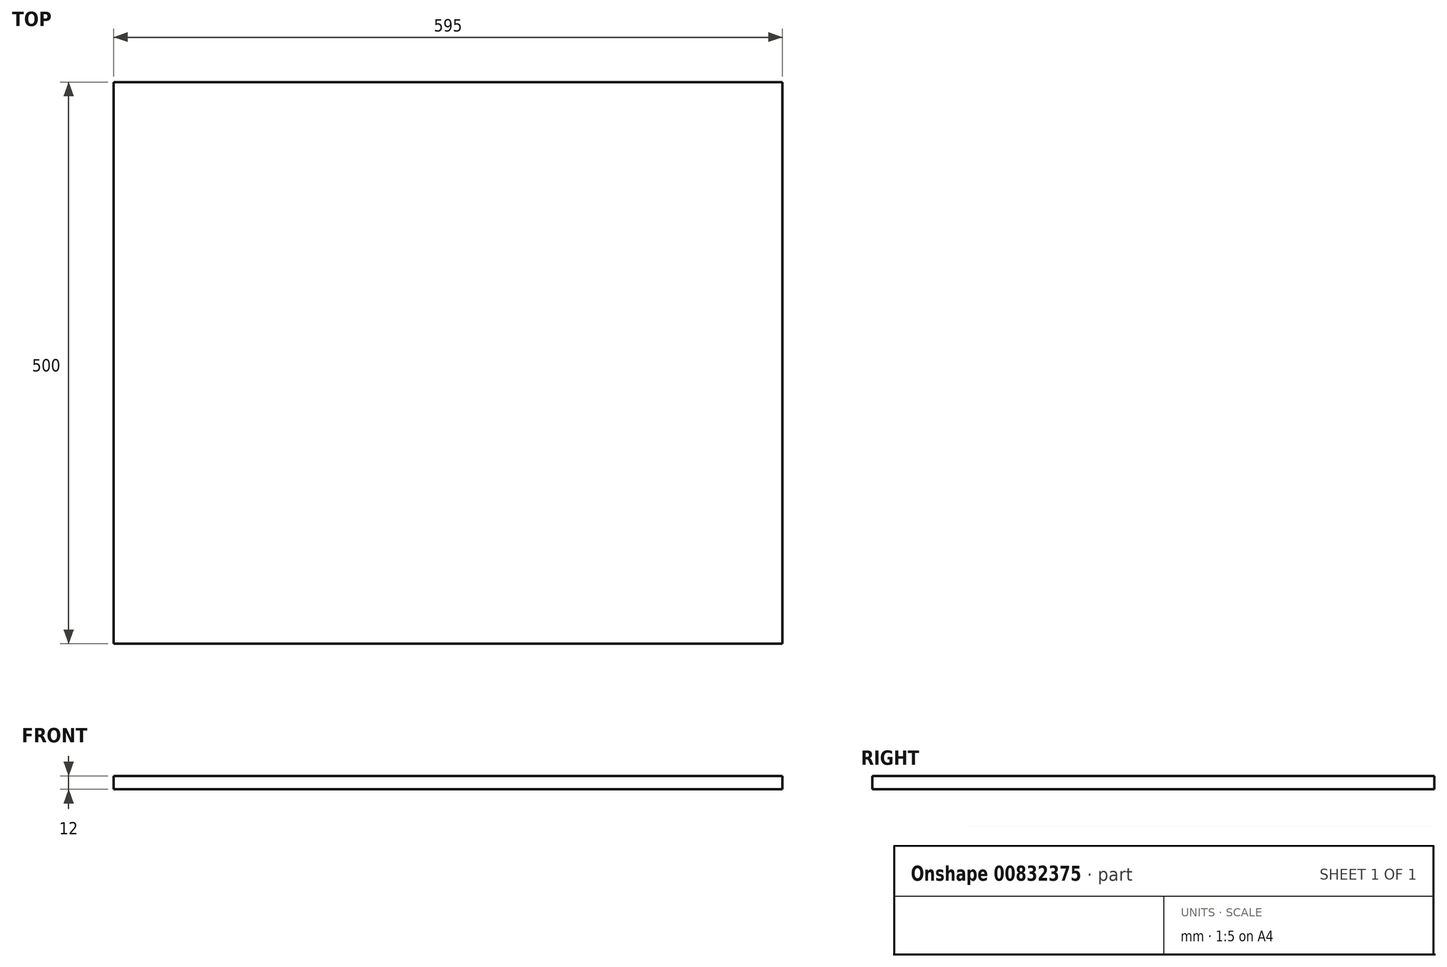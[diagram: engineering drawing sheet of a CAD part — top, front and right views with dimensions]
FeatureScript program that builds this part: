
annotation { "Feature Type Name" : "Feature", "Feature Type Description" : "" }
export const myFeature = defineFeature(function(context is Context, id is Id, definition is map)
    precondition{}
    {
        {
            var Q0;
            Q0=qCreatedBy(makeId("Top.planeOp"),FACE);
            var sketch = newSketch(context, id + "F0", { "sketchPlane" : qUnion([Q0])});
            skLineSegment(sketch, "E0.bottom", {"start": v(0, 0) * mm, "end": v(595, 0) * mm});
            skLineSegment(sketch, "E0.top", {"start": v(0, 500) * mm, "end": v(595, 500) * mm});
            skLineSegment(sketch, "E0.left", {"start": v(0, 0) * mm, "end": v(0, 500) * mm});
            skLineSegment(sketch, "E0.right", {"start": v(595, 0) * mm, "end": v(595, 500) * mm});
            skSolve(sketch);
        }
        {
            var Q0;
            Q0=makeQuery(id+"F0.imprint","IMPRINT",FACE,{"disambiguationData":[TD([[makeQuery(id+"F0.imprint","IMPRINT",EDGE,{"derivedFrom":sQuery(id+"F0.wireOp",EDGE,"E0.bottom")}),1.0]])]});
            extrude(context, id + "F1", {"entities" : qUnion([Q0]), "depth" : 12 * mm, "offsetDistance" : 25 * mm});
        }
    });
